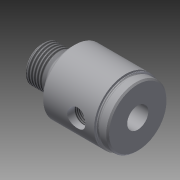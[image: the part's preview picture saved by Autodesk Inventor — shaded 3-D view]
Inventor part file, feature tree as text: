
AUTODESK INVENTOR PART (.ipt)
format: ipt  version: 2014 SP2 (Build 180246200, 246)  size: 255,488 bytes
history: native  units: in
note: dims shown in document units (in); Inventor stores cm internally (conversion verified against a paired STEP export)
features: other x119, sketch x5, revolve x4, thread x2, hole x1
ambient origin geometry x8: Origin, YZ Plane, XZ Plane, XY Plane, X Axis, Y Axis, Z Axis, Center Point
bodies: Solid1 (feature_tree)
feature tree (131):
  revolve  "Revolution1"  [1 undecoded]
  thread  "Thread1"  [1 undecoded]
  revolve  "Revolution2"  Angle=360.0deg
  hole  "Hole1"  [1 undecoded]
  revolve  "Revolution3"  [1 undecoded]
  thread  "Thread2"  [1 undecoded]
  revolve  "Revolution4"  [1 undecoded]
  other  "dp1_XY"
  other  "dp1_YZ"
  other  "dp1_ZX"
  other  "dp1_X"
  other  "dp1_Y"
  other  "dp1_Z"
  other  "dp1_Center"
  other  "dp2_XY"
  other  "dp2_YZ"
  other  "dp2_ZX"
  other  "dp2_X"
  other  "dp2_Y"
  other  "dp2_Z"
  other  "dp2_Center"
  other  "hh_XY"
  other  "hh_YZ"
  other  "hh_ZX"
  other  "hh_X"
  other  "hh_Y"
  other  "hh_Z"
  other  "hh_Center"
  other  "port_XY"
  other  "port_YZ"
  other  "port_ZX"
  other  "port_X"
  other  "port_Y"
  other  "port_Z"
  other  "port_Center"
  other  "rod_guide_XY"
  other  "rod_guide_YZ"
  other  "rod_guide_ZX"
  other  "rod_guide_X"
  other  "rod_guide_Y"
  other  "rod_guide_Z"
  other  "rod_guide_Center"
  other  "s1_XY"
  other  "s1_YZ"
  other  "s1_ZX"
  other  "s1_X"
  other  "s1_Y"
  other  "s1_Z"
  other  "s1_Center"
  other  "s2_XY"
  other  "s2_YZ"
  other  "s2_ZX"
  other  "s2_X"
  other  "s2_Y"
  other  "s2_Z"
  other  "s2_Center"
  other  "t1_XY"
  other  "t1_YZ"
  other  "t1_ZX"
  other  "t1_X"
  other  "t1_Y"
  other  "t1_Z"
  other  "t1_Center"
  other  "t111_XY"
  other  "t111_YZ"
  other  "t111_ZX"
  other  "t111_X"
  other  "t111_Y"
  other  "t111_Z"
  other  "t111_Center"
  other  "to_foot_bracket_XY"
  other  "to_foot_bracket_YZ"
  other  "to_foot_bracket_ZX"
  other  "to_foot_bracket_X"
  other  "to_foot_bracket_Y"
  other  "to_foot_bracket_Z"
  other  "to_foot_bracket_Center"
  other  "to_nut_XY"
  other  "to_nut_YZ"
  other  "to_nut_ZX"
  other  "to_nut_X"
  other  "to_nut_Y"
  other  "to_nut_Z"
  other  "to_nut_Center"
  other  "to_rod_XY"
  other  "to_rod_YZ"
  other  "to_rod_ZX"
  other  "to_rod_X"
  other  "to_rod_Y"
  other  "to_rod_Z"
  other  "to_rod_Center"
  other  "to_screw_XY"
  other  "to_screw_YZ"
  other  "to_screw_ZX"
  other  "to_screw_X"
  other  "to_screw_Y"
  other  "to_screw_Z"
  other  "to_screw_Center"
  other  "to_trunnion_brackets_XY"
  other  "to_trunnion_brackets_YZ"
  other  "to_trunnion_brackets_ZX"
  other  "to_trunnion_brackets_X"
  other  "to_trunnion_brackets_Y"
  other  "to_trunnion_brackets_Z"
  other  "to_trunnion_brackets_Center"
  other  "to_trunnion_brackets1_XY"
  other  "to_trunnion_brackets1_YZ"
  other  "to_trunnion_brackets1_ZX"
  other  "to_trunnion_brackets1_X"
  other  "to_trunnion_brackets1_Y"
  other  "to_trunnion_brackets1_Z"
  other  "to_trunnion_brackets1_Center"
  other  "to_trunnion_brackets2_XY"
  other  "to_trunnion_brackets2_YZ"
  other  "to_trunnion_brackets2_ZX"
  other  "to_trunnion_brackets2_X"
  other  "to_trunnion_brackets2_Y"
  other  "to_trunnion_brackets2_Z"
  other  "to_trunnion_brackets2_Center"
  other  "to_tube_XY"
  other  "to_tube_YZ"
  other  "to_tube_ZX"
  other  "to_tube_X"
  other  "to_tube_Y"
  other  "to_tube_Z"
  other  "to_tube_Center"
  sketch  "Sketch_2"  dims[d0=360.0deg d1=0.3315in d2=0.0in d3=360.0deg]
  sketch  "Sketch_3"  dims[d4=0.442in d5=0.75in d6=0.502in d7=0.25in d8=90.0deg d9=2.0in d10=0.0in d11=360.0deg]
  sketch  "Sketch3"  dims[d12=0.2251in d13=0.0in d14=360.0deg]
  sketch  "Sketch_40"  dims[d15=0.0in d16=0.0in d17=0.0in d18=0.0in d19=0.0in d20=0.0in]
  sketch  "Sketch_47"
note: 6 required parameter values undecoded (feature->parameter linkage not recoverable at this tier; creation-order binding heuristic only, values carry confidence <= 0.55)